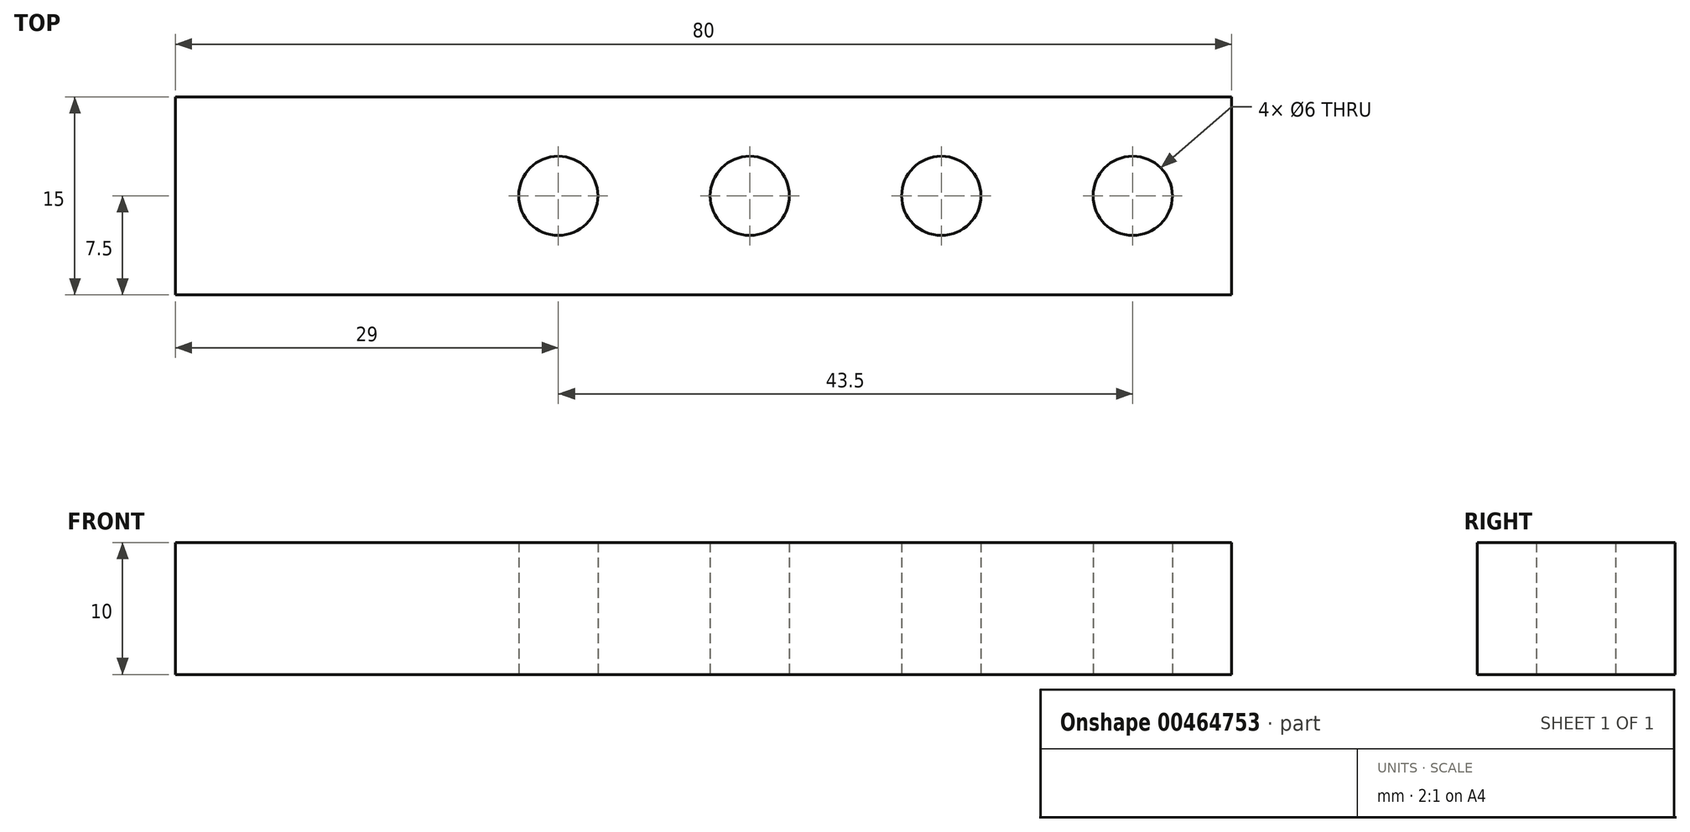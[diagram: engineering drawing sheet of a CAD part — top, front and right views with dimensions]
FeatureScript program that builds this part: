
annotation { "Feature Type Name" : "Feature", "Feature Type Description" : "" }
export const myFeature = defineFeature(function(context is Context, id is Id, definition is map)
    precondition{}
    {
        {
            var Q0;
            Q0=qCreatedBy(makeId("Top.planeOp"),FACE);
            var sketch = newSketch(context, id + "F0", { "sketchPlane" : qUnion([Q0])});
            skLineSegment(sketch, "E0.bottom", {"start": v(0, 0) * mm, "end": v(80, 0) * mm});
            skLineSegment(sketch, "E0.top", {"start": v(0, 15) * mm, "end": v(80, 15) * mm});
            skLineSegment(sketch, "E0.left", {"start": v(0, 0) * mm, "end": v(0, 15) * mm});
            skLineSegment(sketch, "E0.right", {"start": v(80, 0) * mm, "end": v(80, 15) * mm});
            skLineSegment(sketch, "E1", {"start": v(29, 15) * mm, "end": v(29, 0) * mm, "construction": true});
            skCircle(sketch, "E2", {"center": v(29, 7.5) * mm, "radius": 3 * mm});
            skLineSegment(sketch, "E3", {"start": v(0, 7.5) * mm, "end": v(80, 7.5) * mm, "construction": true});
            skCircle(sketch, "E4", {"center": v(29, 7.5) * mm, "radius": 6.75 * mm, "construction": true});
            skCircle(sketch, "E5.1.0.0", {"center": v(43.5, 7.5) * mm, "radius": 3 * mm});
            skCircle(sketch, "E5.1.0.1", {"center": v(43.5, 7.5) * mm, "radius": 6.75 * mm, "construction": true});
            skCircle(sketch, "E5.2.0.0", {"center": v(58, 7.5) * mm, "radius": 3 * mm});
            skCircle(sketch, "E5.2.0.1", {"center": v(58, 7.5) * mm, "radius": 6.75 * mm, "construction": true});
            skCircle(sketch, "E5.3.0.0", {"center": v(72.5, 7.5) * mm, "radius": 3 * mm});
            skCircle(sketch, "E5.3.0.1", {"center": v(72.5, 7.5) * mm, "radius": 6.75 * mm, "construction": true});
            skLineSegment(sketch, "E5.direction1", {"start": v(29, 7.5) * mm, "end": v(43.5, 7.5) * mm, "construction": true});
            skSolve(sketch);
        }
        {
            var Q0;
            Q0 = qSketchRegion(id + "F0", true);
            extrude(context, id + "F1", {"entities" : qUnion([Q0]), "depth" : 10 * mm});
        }
    });
